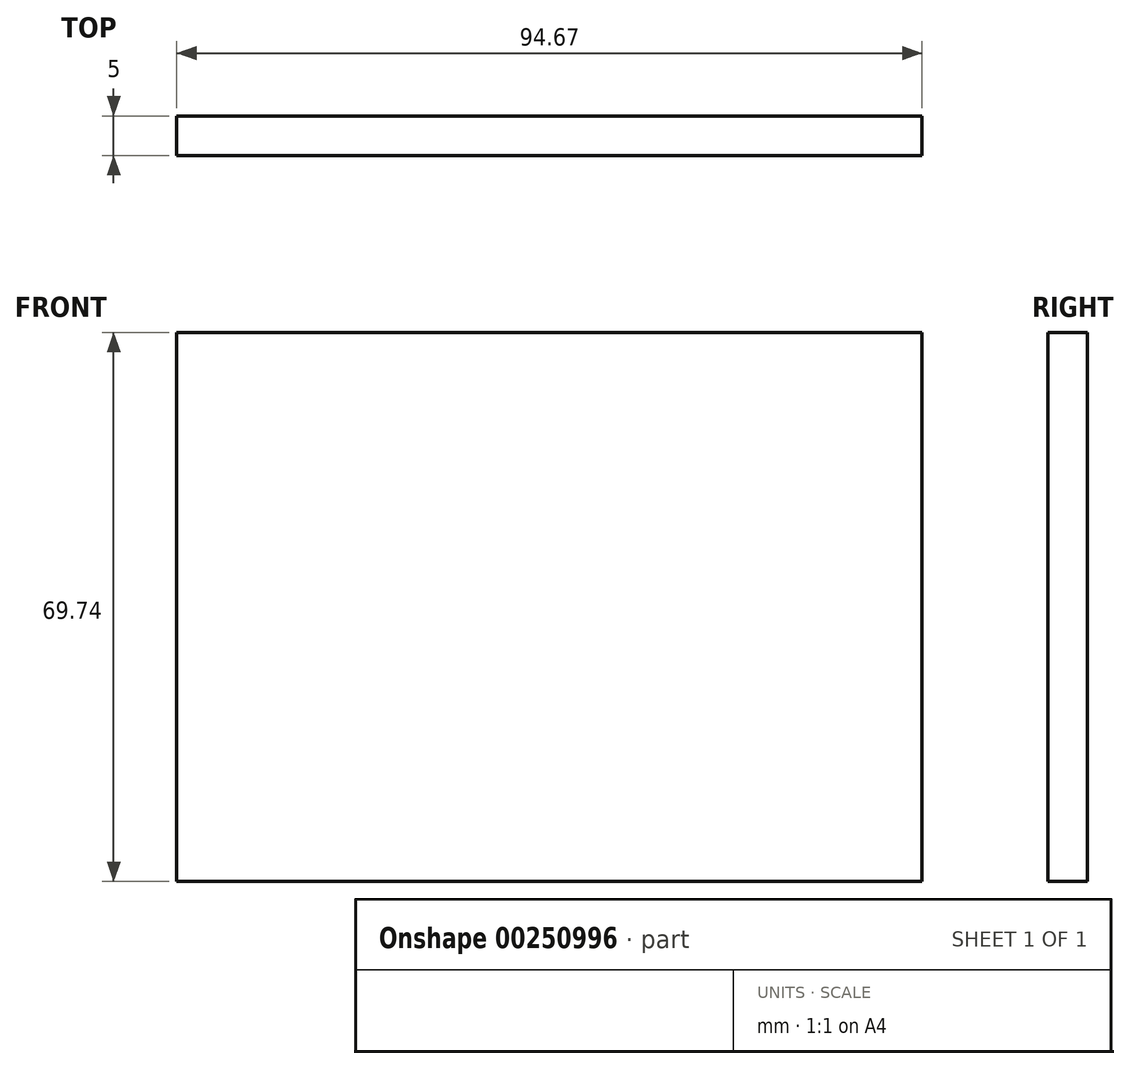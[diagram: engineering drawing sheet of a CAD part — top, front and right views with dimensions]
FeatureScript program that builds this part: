
annotation { "Feature Type Name" : "Feature", "Feature Type Description" : "" }
export const myFeature = defineFeature(function(context is Context, id is Id, definition is map)
    precondition{}
    {
        {
            var Q0;
            Q0=qCreatedBy(makeId("Front.planeOp"),FACE);
            var sketch = newSketch(context, id + "F0", { "sketchPlane" : qUnion([Q0])});
            skLineSegment(sketch, "E0.bottom", {"start": v(-51.61, 27.53) * mm, "end": v(43.06, 27.53) * mm});
            skLineSegment(sketch, "E0.top", {"start": v(-51.61, -42.21) * mm, "end": v(43.06, -42.21) * mm});
            skLineSegment(sketch, "E0.left", {"start": v(-51.61, 27.53) * mm, "end": v(-51.61, -42.21) * mm});
            skLineSegment(sketch, "E0.right", {"start": v(43.06, 27.53) * mm, "end": v(43.06, -42.21) * mm});
            skSolve(sketch);
        }
        {
            var Q0;
            Q0=makeQuery(id+"F0.imprint","IMPRINT",FACE,{"disambiguationData":[TD([[makeQuery(id+"F0.imprint","IMPRINT",EDGE,{"derivedFrom":sQuery(id+"F0.wireOp",EDGE,"E0.bottom")}),-1.0]])]});
            extrude(context, id + "F1", {"entities" : qUnion([Q0]), "endBound" : BoundingType.SYMMETRIC, "depth" : 5 * mm});
        }
    });
